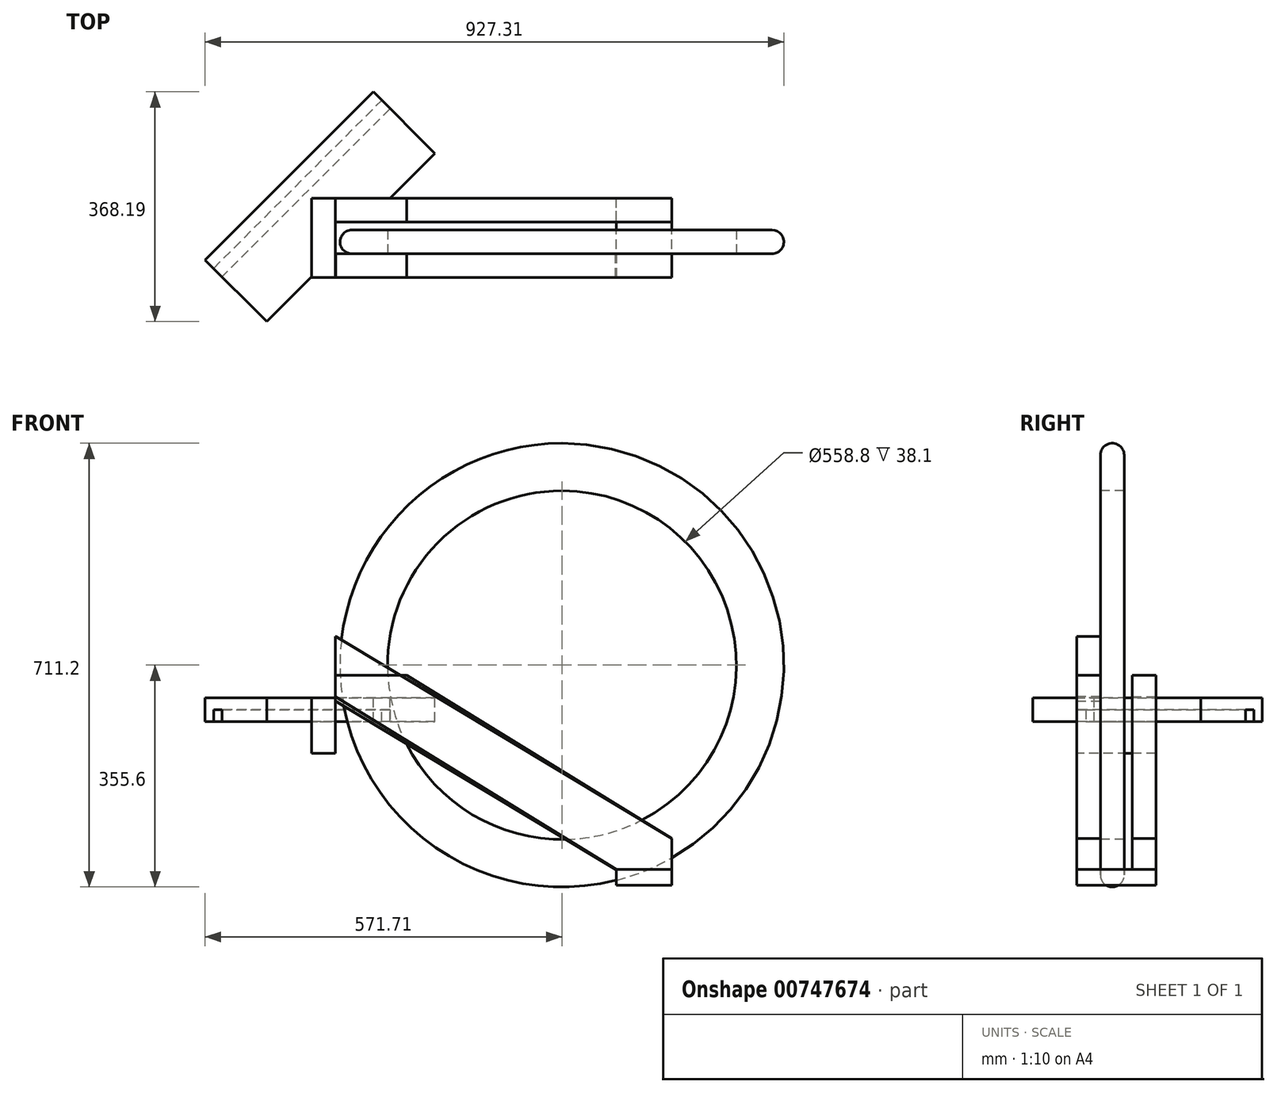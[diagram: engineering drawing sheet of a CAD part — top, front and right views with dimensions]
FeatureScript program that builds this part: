
annotation { "Feature Type Name" : "Feature", "Feature Type Description" : "" }
export const myFeature = defineFeature(function(context is Context, id is Id, definition is map)
    precondition{}
    {
        {
            var Q0;
            Q0=qCreatedBy(makeId("Front.planeOp"),FACE);
            var sketch = newSketch(context, id + "F0", { "sketchPlane" : qUnion([Q0])});
            skLineSegment(sketch, "E0", {"start": v(449.1, 35.22) * mm, "end": v(539.06, 35.22) * mm});
            skLineSegment(sketch, "E1", {"start": v(539.06, 35.22) * mm, "end": v(539.06, 84.88) * mm});
            skLineSegment(sketch, "E2", {"start": v(0.65, 408.38) * mm, "end": v(0, 408.38) * mm});
            skLineSegment(sketch, "E3", {"start": v(0, 408.38) * mm, "end": v(0, 305.06) * mm});
            skLineSegment(sketch, "E4", {"start": v(0, 305.06) * mm, "end": v(449.1, 35.22) * mm});
            skLineSegment(sketch, "E5", {"start": v(539.06, 84.88) * mm, "end": v(0.65, 408.38) * mm});
            skPoint(sketch, "E6.orphan", {"position": v(539.06, 134.53) * mm});
            skPoint(sketch, "E7.orphan", {"position": v(1.3, 408.38) * mm});
            skSolve(sketch);
        }
        {
            var Q0;
            Q0=makeQuery(id+"F0.imprint","IMPRINT",FACE,{"disambiguationData":[TD([[makeQuery(id+"F0.imprint","IMPRINT",EDGE,{"derivedFrom":sQuery(id+"F0.wireOp",EDGE,"E0")}),1.0]])]});
            extrude(context, id + "F1", {"entities" : qUnion([Q0]), "depth" : 38.1 * mm, "offsetDistance" : 25.4 * mm});
        }
        {
            var Q0;
            Q0=makeQuery(id+"F1.opExtrude","SWEPT_FACE",FACE,{"disambiguationData":[OSD([sQuery(id+"F0.wireOp",EDGE,"E0")])]});
            var sketch = newSketch(context, id + "F2", { "sketchPlane" : qUnion([Q0])});
            skLineSegment(sketch, "E8.bottom", {"start": v(539.06, 38.1) * mm, "end": v(450.16, 38.1) * mm});
            skLineSegment(sketch, "E8.top", {"start": v(539.06, -88.9) * mm, "end": v(450.16, -88.9) * mm});
            skLineSegment(sketch, "E8.left", {"start": v(539.06, 38.1) * mm, "end": v(539.06, -88.9) * mm});
            skLineSegment(sketch, "E8.right", {"start": v(450.16, 38.1) * mm, "end": v(450.16, -88.9) * mm});
            skSolve(sketch);
        }
        {
            var Q0;
            Q0 = qSketchRegion(id + "F2", true);
            extrude(context, id + "F3", {"entities" : qUnion([Q0]), "depth" : 25.4 * mm, "offsetDistance" : 25.4 * mm});
        }
        {
            var Q0;
            Q0=makeQuery(id+"F3.opExtrude","SWEPT_FACE",FACE,{"disambiguationData":[OSD([sQuery(id+"F2.wireOp",EDGE,"E8.top")])]});
            var sketch = newSketch(context, id + "F4", { "sketchPlane" : qUnion([Q0])});
            skLineSegment(sketch, "E9.top", {"start": v(-539.06, 124.12) * mm, "end": v(-450.16, 124.12) * mm});
            skLineSegment(sketch, "E9.left", {"start": v(-539.06, 35.22) * mm, "end": v(-539.06, 124.12) * mm});
            skLineSegment(sketch, "E9.right", {"start": v(-450.16, 35.22) * mm, "end": v(-450.16, 124.12) * mm});
            skLineSegment(sketch, "E10", {"start": v(-450.16, 35.22) * mm, "end": v(-539.06, 35.22) * mm});
            skSolve(sketch);
        }
        {
            var Q0;
            Q0=makeQuery(id+"F3.boolean.opBoolean","MERGE",FACE,{"derivedFrom":[makeQuery(id+"F1.opExtrude","CAP_FACE",FACE,{"disambiguationData":[OSD([sQuery(id+"F0.wireOp",EDGE,"E0"),sQuery(id+"F0.wireOp",EDGE,"E1"),sQuery(id+"F0.wireOp",EDGE,"9WPtiAUY-CqDA-4t2l-u8TL-ciBx688L6UC3"),sQuery(id+"F0.wireOp",EDGE,"ayKcAvuQ-uz7o-ofrZ-9PYY-mscUa0N6uuzY"),sQuery(id+"F0.wireOp",EDGE,"E2"),sQuery(id+"F0.wireOp",EDGE,"E3")])],"isStart":false}),makeQuery(id+"F3.opExtrude","SWEPT_FACE",FACE,{"disambiguationData":[OSD([sQuery(id+"F2.wireOp",EDGE,"E8.bottom")])]})]});
            var sketch = newSketch(context, id + "F5", { "sketchPlane" : qUnion([Q0])});
            skLineSegment(sketch, "E11.bottom", {"start": v(0, 310.14) * mm, "end": v(-38.1, 310.14) * mm});
            skLineSegment(sketch, "E11.top", {"start": v(0, 221.24) * mm, "end": v(-38.1, 221.24) * mm});
            skLineSegment(sketch, "E11.left", {"start": v(0, 310.14) * mm, "end": v(0, 221.24) * mm});
            skLineSegment(sketch, "E11.right", {"start": v(-38.1, 310.14) * mm, "end": v(-38.1, 221.24) * mm});
            skSolve(sketch);
        }
        {
            var Q0;
            Q0 = qSketchRegion(id + "F5", true);
            extrude(context, id + "F6", {"entities" : qUnion([Q0]), "oppositeDirection" : true, "depth" : 127 * mm, "offsetDistance" : 25.4 * mm});
        }
        {
            var Q0;
            Q0=makeQuery(id+"F6.opExtrude","SWEPT_FACE",FACE,{"disambiguationData":[OSD([sQuery(id+"F5.wireOp",EDGE,"E11.left")])]});
            var sketch = newSketch(context, id + "F7", { "sketchPlane" : qUnion([Q0])});
            skLineSegment(sketch, "E12.bottom", {"start": v(88.9, 310.14) * mm, "end": v(50.8, 310.14) * mm});
            skLineSegment(sketch, "E12.top", {"start": v(88.9, 221.24) * mm, "end": v(50.8, 221.24) * mm});
            skLineSegment(sketch, "E12.left", {"start": v(88.9, 310.14) * mm, "end": v(88.9, 221.24) * mm});
            skLineSegment(sketch, "E12.right", {"start": v(50.8, 310.14) * mm, "end": v(50.8, 221.24) * mm});
            skSolve(sketch);
        }
        {
            var Q0;
            Q0=makeQuery(id+"F1.opExtrude","CAP_FACE",FACE,{"disambiguationData":[OSD([sQuery(id+"F0.wireOp",EDGE,"E0"),sQuery(id+"F0.wireOp",EDGE,"E1"),sQuery(id+"F0.wireOp",EDGE,"9WPtiAUY-CqDA-4t2l-u8TL-ciBx688L6UC3"),sQuery(id+"F0.wireOp",EDGE,"ayKcAvuQ-uz7o-ofrZ-9PYY-mscUa0N6uuzY"),sQuery(id+"F0.wireOp",EDGE,"E2"),sQuery(id+"F0.wireOp",EDGE,"E3")])],"isStart":true});
            var sketch = newSketch(context, id + "F8", { "sketchPlane" : qUnion([Q0])});
            skCircle(sketch, "E13", {"center": v(-362.99, 362.64) * mm, "radius": 355.6 * mm});
            skCircle(sketch, "E14", {"center": v(-362.99, 362.64) * mm, "radius": 279.4 * mm});
            skSolve(sketch);
        }
        {
            var Q0;
            Q0 = qSketchRegion(id + "F8", true);
            extrude(context, id + "F9", {"entities" : qUnion([Q0]), "depth" : 38.1 * mm, "offsetDistance" : 25.4 * mm});
        }
        {
            var Q0;
            Q0=makeQuery(id+"F9.opExtrude","CAP_EDGE",EDGE,{"disambiguationData":[OSD([sQuery(id+"F8.wireOp",EDGE,"E13")])],"isStart":true});
            var Q1;
            Q1=makeQuery(id+"F9.opExtrude","CAP_EDGE",EDGE,{"disambiguationData":[OSD([sQuery(id+"F8.wireOp",EDGE,"E13")])],"isStart":false});
            fillet(context, id + "F10", {"entities" : qUnion([Q0, Q1]), "radius" : 19.05 * mm, "tangentPropagation" : true, "allowEdgeOverflow" : false});
        }
        {
            var Q0;
            Q0=makeQuery(id+"F6.opExtrude","SWEPT_FACE",FACE,{"disambiguationData":[OSD([sQuery(id+"F5.wireOp",EDGE,"E11.bottom")])]});
            var sketch = newSketch(context, id + "F11", { "sketchPlane" : qUnion([Q0])});
            skLineSegment(sketch, "E15", {"start": v(-208.72, -9.88) * mm, "end": v(60.68, 259.52) * mm});
            skLineSegment(sketch, "E16", {"start": v(60.68, 259.52) * mm, "end": v(159.47, 160.74) * mm});
            skLineSegment(sketch, "E17", {"start": v(159.47, 160.74) * mm, "end": v(87.62, 88.9) * mm});
            skLineSegment(sketch, "E18", {"start": v(87.62, 88.9) * mm, "end": v(-38.1, 88.9) * mm});
            skLineSegment(sketch, "E19", {"start": v(-38.1, 88.9) * mm, "end": v(-38.1, -36.82) * mm});
            skLineSegment(sketch, "E20", {"start": v(-38.1, -36.82) * mm, "end": v(-109.94, -108.67) * mm});
            skLineSegment(sketch, "E21", {"start": v(-109.94, -108.67) * mm, "end": v(-208.72, -9.88) * mm});
            skSolve(sketch);
        }
        {
            var Q0;
            Q0 = qSketchRegion(id + "F11", true);
            extrude(context, id + "F12", {"entities" : qUnion([Q0]), "oppositeDirection" : true, "depth" : 38.1 * mm, "offsetDistance" : 25.4 * mm});
        }
        {
            var Q0;
            Q0=makeQuery(id+"F12.opExtrude","CAP_FACE",FACE,{"disambiguationData":[OSD([sQuery(id+"F11.wireOp",EDGE,"E15"),sQuery(id+"F11.wireOp",EDGE,"E16"),sQuery(id+"F11.wireOp",EDGE,"E17"),sQuery(id+"F11.wireOp",EDGE,"E18"),sQuery(id+"F11.wireOp",EDGE,"E19"),sQuery(id+"F11.wireOp",EDGE,"E20"),sQuery(id+"F11.wireOp",EDGE,"E21")])],"isStart":false});
            var sketch = newSketch(context, id + "F13", { "sketchPlane" : qUnion([Q0])});
            skLineSegment(sketch, "E22", {"start": v(-195.25, 23.35) * mm, "end": v(74.15, -246.05) * mm});
            skLineSegment(sketch, "E23", {"start": v(74.15, -246.05) * mm, "end": v(87.62, -232.58) * mm});
            skLineSegment(sketch, "E24", {"start": v(87.62, -232.58) * mm, "end": v(-181.78, 36.82) * mm});
            skLineSegment(sketch, "E25", {"start": v(-181.78, 36.82) * mm, "end": v(-195.25, 23.35) * mm});
            skSolve(sketch);
        }
        {
            var Q0;
            Q0 = qSketchRegion(id + "F13", true);
            extrude(context, id + "F14", {"entities" : qUnion([Q0]), "operationType" : NewBodyOperationType.REMOVE, "oppositeDirection" : true, "depth" : 19.05 * mm, "offsetDistance" : 25.4 * mm});
        }
        {
            var Q0;
            Q0=makeQuery(id+"F3.opExtrude","SWEPT_FACE",FACE,{"disambiguationData":[OSD([sQuery(id+"F2.wireOp",EDGE,"E8.top")])]});
            var sketch = newSketch(context, id + "F15", { "sketchPlane" : qUnion([Q0])});
            skLineSegment(sketch, "E26", {"start": v(-539.06, 35.22) * mm, "end": v(-450.16, 35.22) * mm});
            skLineSegment(sketch, "E27", {"start": v(-450.16, 35.22) * mm, "end": v(0, 312.35) * mm});
            skLineSegment(sketch, "E28", {"start": v(0, 312.35) * mm, "end": v(0, 346.38) * mm});
            skLineSegment(sketch, "E29", {"start": v(-114.3, 346.38) * mm, "end": v(-539.06, 84.88) * mm});
            skLineSegment(sketch, "E30", {"start": v(-539.06, 84.88) * mm, "end": v(-539.06, 35.22) * mm});
            skLineSegment(sketch, "E31", {"start": v(0, 346.38) * mm, "end": v(-114.3, 346.38) * mm});
            skSolve(sketch);
        }
        {
            var Q0;
            Q0 = qSketchRegion(id + "F15", true);
            extrude(context, id + "F16", {"entities" : qUnion([Q0]), "oppositeDirection" : true, "depth" : 38.1 * mm, "offsetDistance" : 25.4 * mm});
        }
        {
            var Q0;
            Q0=makeQuery(id+"F3.opExtrude","SWEPT_FACE",FACE,{"disambiguationData":[OSD([sQuery(id+"F2.wireOp",EDGE,"E8.bottom")])]});
            var sketch = newSketch(context, id + "F17", { "sketchPlane" : qUnion([Q0])});
            skSolve(sketch);
        }
        {
            var Q0;
            {var subQ0=sQuery(id+"F2.wireOp",EDGE,"E8.bottom");Q0=makeQuery(id+"F17.imprint","IMPRINT",FACE,{"disambiguationData":[TD([[makeQuery(id+"F17.imprint","IMPRINT",EDGE,{"derivedFrom":makeQuery(id+"F3.opExtrude","CAP_EDGE",EDGE,{"disambiguationData":[OSD([subQ0])],"isStart":true})}),-1.0]])]});}
            var sketch = newSketch(context, id + "F18", { "sketchPlane" : qUnion([Q0])});
            skLineSegment(sketch, "E32.0.0", {"start": v(539.06, 84.88) * mm, "end": v(114.3, 346.38) * mm});
            skLineSegment(sketch, "E32.0.1", {"start": v(114.3, 346.38) * mm, "end": v(0, 346.38) * mm});
            skLineSegment(sketch, "E32.0.2", {"start": v(0, 346.38) * mm, "end": v(0, 312.35) * mm});
            skLineSegment(sketch, "E32.0.3", {"start": v(0, 312.35) * mm, "end": v(450.16, 35.22) * mm});
            skLineSegment(sketch, "E32.0.4", {"start": v(450.16, 35.22) * mm, "end": v(539.06, 35.22) * mm});
            skLineSegment(sketch, "E32.0.5", {"start": v(539.06, 35.22) * mm, "end": v(539.06, 84.88) * mm});
            skSolve(sketch);
        }
        {
            var Q0;
            Q0 = qSketchRegion(id + "F18", true);
            extrude(context, id + "F19", {"entities" : qUnion([Q0]), "oppositeDirection" : true, "depth" : 38.1 * mm, "offsetDistance" : 25.4 * mm});
        }
    });
